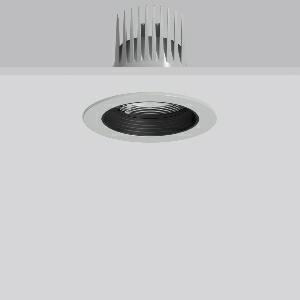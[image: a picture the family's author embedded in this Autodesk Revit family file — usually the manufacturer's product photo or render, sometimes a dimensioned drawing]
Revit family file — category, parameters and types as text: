
# Revit family: heledon_maxi_e_901762_004_2_1ade
name_source: partatom
category: Lighting Fixtures
units: mm (PartAtom-declared; Revit-internal decimal feet)

## family parameters
Cut with Voids When Loaded = No
Host = Face
Light Source = No
Part Type = Normal
Room Calculation Point = No
Round Connector Dimension = Use Diameter
Shared = No

## types (1)
- HELEDON maxi E (1 x LED Modul 927, 2650 lm, 2700)
    Apparent Load = 25 VA
    Approval mark = CE
    CIE Flux Codes = 96 100 100 100 100
    Color Rendering = 92
    Color Temperature = 2700
    Default Elevation = 1800 mm
    Description = Series: HELEDON maxi
Round recessed downlight. Housing: die-cast aluminium, powder-coated. Black plastic ring and recessed LED to prevent glare from the side. Optical assembly with lens made of plastic (polycarbonate) for the best homogeneous light distribution - can be changed without tools. Best colour rendering index Ra>90. Suitable for Recessed ceiling mounting. Installation without tools thanks to spring fastening system. Including separate LED converter with connecting cable 600 mm.High quality converter without flickering and stroboscopic effect. Through-wiring box (5 pole) available as accessory. The following accessories can be mounted without use of tools: interchangeable lenses, decorative glasses, honeycomb louvre, clear and frosted diffusers, white interchangeable plastic ring. 
Colour: silver
Diameter: 162 mm
Height: 3 mm
Cut-out diameter: 152 mm
Recess height: 200 mm
Luminaire: recess height: 135 mm
Lamp: LED
Socket: without socket
Colour temperature: 2700K
Colour rendering index (CRI): 92
System power: 25 W
Rated luminous flux: 2650 lm
Luminous efficiency: 106 lm/W
Control gear: Regulated power supply
Protection class: II
Type of protection: IP 20
    Height = 0 mm  [stored 0 ft]
    Lamp = 1 x LED Modul 927
    Lamp Light Flux = 2650 lm
    Lamp count = 1
    Length = 162 mm
    Lifetime = 50000 h
    Luminous efficacy = 106 lm/W
    Manufacturer = RZB
    ModVariant = No
    Model = 901762.004.2
    Mounting Place = Ceiling
    Mounting Type = Recessed
    Number of Poles = 1
    OnlyDefault = Yes
    Power Factor = 1
    Product Name = HELEDON maxi E
    Product group = Recessed downlights
    ProductGroupID = 402
    Protection Class = Protection class II
    Protection Degree = IP 20
    RLX_Detail_Level = 1
    RLX_Emergency_Light_Flux = 0 lm
    RLX_Emergency_Type = 0
    RLX_Emergency_Type_DB = No
    RlxData = <blob elided: 119313 chars, md5=e312107d>
    Socket = socket
    Standby Power = 0 W
    System Light Flux = 2650 lm
    System Power = 25 W
    Type Comments = Product without accessories
    Type Image = 901663.004.jpg
    URL = http://relux.com
    VarID = ---
    Voltage = 230 V
    Voltage Range = 220-240 V
    Weight = 0.00 kg
    Width = 0 mm  [stored 0 ft]

note: [stored X ft] marks values corroborated as IEEE doubles in the binary element streams (Revit-internal decimal feet)

## geometry (parser evidence)
native form markers: Blend x4, Sweep x12
no freeform markers — native parametric forms only
